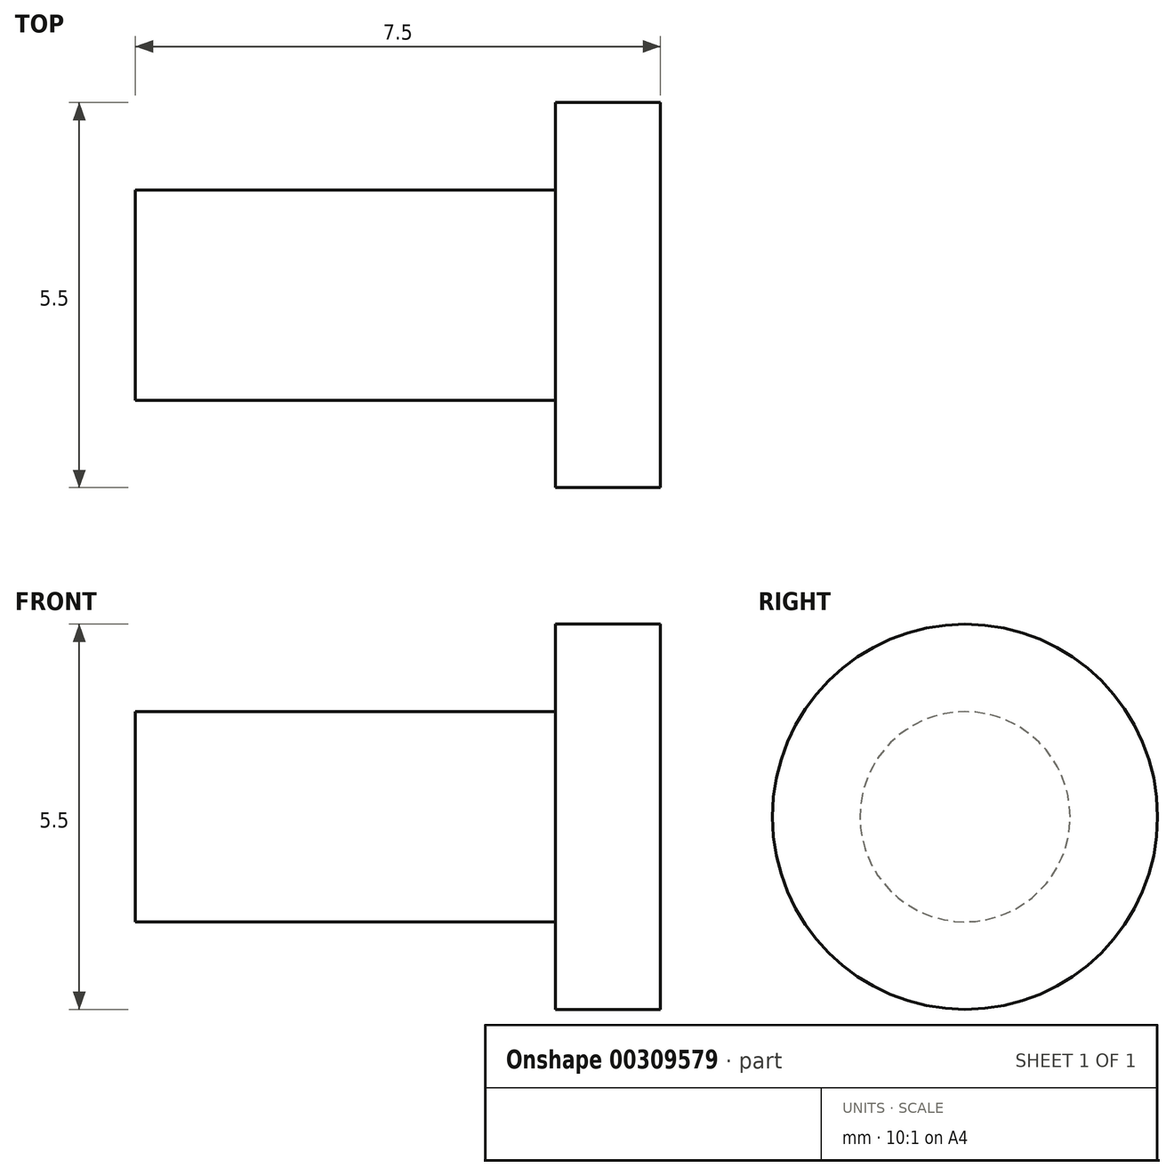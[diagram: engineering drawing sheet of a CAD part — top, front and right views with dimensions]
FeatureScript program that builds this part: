
annotation { "Feature Type Name" : "Feature", "Feature Type Description" : "" }
export const myFeature = defineFeature(function(context is Context, id is Id, definition is map)
    precondition{}
    {
        {
            var Q0;
            Q0=qCreatedBy(makeId("Front.planeOp"),FACE);
            var sketch = newSketch(context, id + "F0", { "sketchPlane" : qUnion([Q0])});
            skLineSegment(sketch, "E0", {"start": v(0, 0) * mm, "end": v(7.5, 0) * mm});
            skLineSegment(sketch, "E1", {"start": v(7.5, 0) * mm, "end": v(7.5, 2.75) * mm});
            skLineSegment(sketch, "E2", {"start": v(7.5, 2.75) * mm, "end": v(6, 2.75) * mm});
            skLineSegment(sketch, "E3", {"start": v(6, 1.5) * mm, "end": v(6, 2.75) * mm});
            skLineSegment(sketch, "E4", {"start": v(6, 1.5) * mm, "end": v(0, 1.5) * mm});
            skLineSegment(sketch, "E5", {"start": v(0, 0) * mm, "end": v(0, 1.5) * mm});
            skSolve(sketch);
        }
        {
            var Q0;
            Q0=makeQuery(id+"F0.imprint","IMPRINT",FACE,{"disambiguationData":[TD([[makeQuery(id+"F0.imprint","IMPRINT",EDGE,{"derivedFrom":sQuery(id+"F0.wireOp",EDGE,"E0")}),1.0]])]});
            var Q1;
            Q1=sQuery(id+"F0.wireOp",EDGE,"E0");
            revolve(context, id + "F1", {"entities" : qUnion([Q0]), "axis" : qUnion([Q1]), "revolveType" : RevolveType.FULL});
        }
    });
